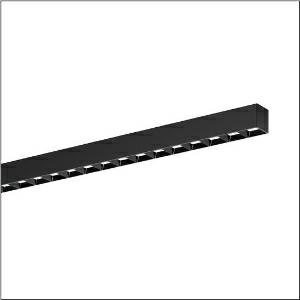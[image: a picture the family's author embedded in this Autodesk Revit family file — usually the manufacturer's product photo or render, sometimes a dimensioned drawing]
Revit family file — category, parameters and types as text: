
# Revit family: silica_r__21_51mx21tat4b_6284
name_source: partatom
category: Lighting Fixtures
units: mm (PartAtom-declared; Revit-internal decimal feet)

## family parameters
Cut with Voids When Loaded = No
Host = Face
Light Source = No
Part Type = Normal
Room Calculation Point = No
Round Connector Dimension = Use Diameter
Shared = No

## types (1)
- --- (1 x LED, 3720 lm, 32.2 W, 6500K)
    Apparent Load = 32 VA
    CIE Flux Codes = 85 99 100 100 100
    Color Rendering = 80
    Color Temperature = 6500K
    Default Elevation = 1800 mm
    Description = Silica® 21, office luminaire, primary light control with darklight reflector, of PMMA, black, CAT 2 (L<= 3000cd/m²), light emission: direct distribution, primary light characteristic: symmetric, installation type: surface-mounted, LED, rated luminous flux: 3.720lm, luminous efficacy: 110lm/W, light colour: 8tw, colour temperature: 2700..6500K, control gear: DALI DT8, with terminal, 3+2-pole, max. 2.5mm², mains connection: 220..240V, AC, 50/60Hz, rated input power: 33.8W, luminaire housing, of aluminium, matt jet black (RAL 9005), length: 1.204mm, width: 53mm, height: 53mm, protection rating (complete): IP20, insulation class (complete): insulation class I (protective earthing), certification: CE, permissible operating ambient temperature: 0..+35°C, standard: EN 50419, packaging unit: 1 piece
    Height = 53 mm
    Lamp = 1 x LED
    Lamp Light Flux = 3720 lm
    Lamp Power = 32.2 W
    Lamp count = 1
    Length = 1204 mm
    Luminous efficacy = 116 lm/W
    Manufacturer = Siteco
    ModVariant = No
    Model = 51MX21TAT4B
    Mounting Place = Ceiling
    Mounting Type = Surface mounted
    Number of Poles = 1
    OnlyDefault = Yes
    Power Factor = 1
    Product Name = Silica® 21
    Product group = office luminaire | ceiling mounted
    ProductGroupID = 302
    Protection Class = Protection class I
    Protection Degree = IP 20
    RLX_Detail_Level = 1
    RLX_Emergency_Light_Flux = 0 lm
    RLX_Emergency_Type = 0
    RLX_Emergency_Type_DB = No
    RlxData = <blob elided: 40001 chars, md5=013ae9d4>
    Socket = socket
    Standby Power = 0 W
    System Light Flux = 3720 lm
    System Power = 32 W
    Type Comments = individual setting
    Type Image = l_1335908.jpg
    URL = http://relux.com
    VarID = @adj_140070
    Voltage = 0 V
    Weight = 0.00 kg
    Width = 53 mm

## geometry (parser evidence)
native form markers: Blend x4, Sweep x10
no freeform markers — native parametric forms only
